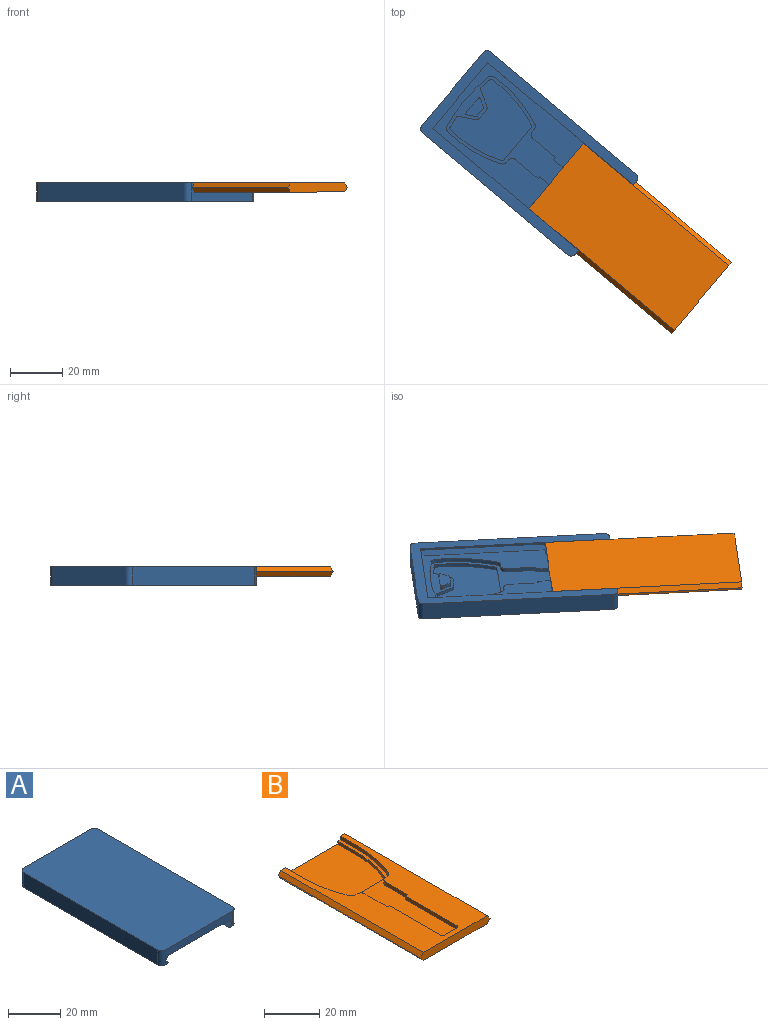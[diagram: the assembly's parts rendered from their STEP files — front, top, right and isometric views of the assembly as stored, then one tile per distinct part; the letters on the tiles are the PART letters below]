
ASSEMBLY  parts=2 mates=1
PART A: 63 faces, bbox 40.5x76.7x7 mm
  f0: plane 36.5x7mm, normal (0,-1,0), area 135.6mm2, adj f1,f5,f6,f55,f56,f57,f58,f59
  f1: plane 76.7x40.5mm, normal (0,0,-1), area 713.4mm2, adj f0,f2,f3,f4,f54,f56,f58,f59
  f2: plane 72.7x7mm, normal (-1,0,0), area 508.9mm2, adj f1,f5,f61,f62
  f3: plane 72.7x7mm, normal (1,0,0), area 508.9mm2, adj f1,f5,f59,f60
  f4: plane 36.5x7mm, normal (0,1,0), area 255.5mm2, adj f1,f5,f60,f61
  f5: plane 76.7x40.5mm, normal (0,0,1), area 3102.9mm2, adj f0,f2,f3,f4,f59,f60,f61,f62
  f6: plane 72.85x32.8mm, normal (0,0,-1), area 1328.2mm2, adj f0,f7,f8,f9,f10,f11,f12,f13
  f7: cylinder r=62.21mm len=24.24mm, axis (0,0,-1), area 37.8mm2, adj f6,f8,f34,f35
  f8: cylinder r=2.1mm len=1.9mm, axis (0,0,-1), area 4.2mm2, adj f6,f7,f9,f35
  f9: cylinder r=50.1mm len=23.22mm, axis (0,0,-1), area 36.8mm2, adj f6,f8,f10,f35
  f10: cylinder r=2.1mm len=1.94mm, axis (0,0,-1), area 3.8mm2, adj f6,f9,f11,f35
  f11: plane 1.55x0.95mm, normal (0,1,0), area 1.5mm2, adj f6,f10,f12,f35
  f12: cylinder r=1.9mm len=1.9mm, axis (0,0,-1), area 4.6mm2, adj f6,f11,f13,f35
  f13: plane 11.4x1.55mm, normal (1,0,0), area 17.7mm2, adj f6,f12,f14,f35
  f14: plane 1.55x1.05mm, normal (0,1,0), area 1.6mm2, adj f6,f13,f15,f35
  f15: plane 26.1x1.55mm, normal (1,0,0), area 40.5mm2, adj f6,f14,f16,f35
  f16: cylinder r=1.1mm len=1.55mm, axis (0,0,-1), area 2.7mm2, adj f6,f15,f17,f35
  f17: plane 6.2x1.55mm, normal (0,1,0), area 9.6mm2, adj f6,f16,f18,f35
  f18: cylinder r=1.1mm len=1.55mm, axis (0,0,-1), area 2.7mm2, adj f6,f17,f19,f35
  f19: plane 26.1x1.55mm, normal (-1,0,0), area 40.5mm2, adj f6,f18,f20,f35
  f20: plane 1.55x1.05mm, normal (0,1,0), area 1.6mm2, adj f6,f19,f21,f35
  f21: plane 11.4x1.55mm, normal (-1,0,0), area 17.7mm2, adj f6,f20,f22,f35
  f22: cylinder r=1.9mm len=1.9mm, axis (0,0,-1), area 4.6mm2, adj f6,f21,f23,f35
  f23: plane 1.55x0.95mm, normal (0,1,0), area 1.5mm2, adj f6,f22,f24,f35
  f24: cylinder r=2.1mm len=1.94mm, axis (0,0,-1), area 3.8mm2, adj f6,f23,f25,f35
  f25: cylinder r=50.1mm len=23.22mm, axis (0,0,-1), area 36.8mm2, adj f6,f24,f34,f35
  f26: cylinder r=0.4mm len=1.55mm, axis (0,0,-1), area 1.2mm2, adj f27,f33,f35,f53
  f27: cylinder r=58.77mm len=7.42mm, axis (0,0,-1), area 11.5mm2, adj f26,f28,f35,f53
  f28: cylinder r=0.4mm len=1.55mm, axis (0,0,-1), area 1.2mm2, adj f27,f29,f35,f53
  f29: plane 3.18x1.76mm, normal (0.88,-0.48,0), area 5.6mm2, adj f28,f30,f35,f53
  f30: cylinder r=0.4mm len=1.55mm, axis (0,0,-1), area 0.7mm2, adj f29,f31,f35,f53
  f31: plane 3.85x1.55mm, normal (0,-1,0), area 6mm2, adj f30,f32,f35,f53
  f32: cylinder r=0.4mm len=1.55mm, axis (0,0,-1), area 0.7mm2, adj f31,f33,f35,f53
  f33: plane 3.18x1.76mm, normal (-0.88,-0.48,0), area 5.6mm2, adj f26,f32,f35,f53
  f34: cylinder r=2.1mm len=1.9mm, axis (0,0,-1), area 4.2mm2, adj f6,f7,f25,f35
  f35: plane 68.1x27.9mm, normal (0,0,-1), area 539mm2, adj f7,f8,f9,f10,f11,f12,f13,f14
  f36: cylinder r=60.91mm len=4.59mm, axis (0,0,-1), area 6mm2, adj f35,f37,f51,f52
  f37: cylinder r=0.8mm len=1.3mm, axis (0,0,-1), area 1.4mm2, adj f35,f36,f38,f52
  f38: cylinder r=48.8mm len=22.62mm, axis (0,0,-1), area 30.1mm2, adj f35,f37,f39,f52
  f39: cylinder r=0.8mm len=1.3mm, axis (0,0,-1), area 1.2mm2, adj f35,f38,f40,f52
  f40: plane 16.2x1.3mm, normal (0,1,0), area 21.1mm2, adj f35,f39,f41,f52
  f41: cylinder r=0.8mm len=1.3mm, axis (0,0,-1), area 1.2mm2, adj f35,f40,f42,f52
  f42: cylinder r=48.8mm len=22.62mm, axis (0,0,-1), area 30.1mm2, adj f35,f41,f43,f52
  f43: cylinder r=0.8mm len=1.3mm, axis (0,0,-1), area 1.4mm2, adj f35,f42,f44,f52
  f44: cylinder r=60.91mm len=4.59mm, axis (0,0,-1), area 6mm2, adj f35,f43,f45,f52
  f45: cylinder r=0.6mm len=1.3mm, axis (0,0,-1), area 0.9mm2, adj f35,f44,f46,f52
  f46: plane 5.92x3.27mm, normal (0.88,-0.48,0), area 8.8mm2, adj f35,f45,f47,f52
  f47: cylinder r=1.7mm len=1.49mm, axis (0,0,-1), area 2.4mm2, adj f35,f46,f48,f52
  f48: plane 3.85x1.3mm, normal (0,-1,0), area 5mm2, adj f35,f47,f49,f52
  f49: cylinder r=1.7mm len=1.49mm, axis (0,0,-1), area 2.4mm2, adj f35,f48,f50,f52
  f50: plane 5.92x3.27mm, normal (-0.88,-0.48,0), area 8.8mm2, adj f35,f49,f51,f52
  f51: cylinder r=0.6mm len=1.3mm, axis (0,0,-1), area 0.9mm2, adj f35,f36,f50,f52
  f52: plane 25.3x24.57mm, normal (0,0,-1), area 496mm2, adj f36,f37,f38,f39,f40,f41,f42,f43
  f53: plane 8.17x4.1mm, normal (0,0,-1), area 26.3mm2, adj f26,f27,f28,f29,f30,f31,f32,f33
  f54: plane 35.74x3.5mm, normal (0,-1,0), area 119.9mm2, adj f1,f6,f55,f56,f57,f58
  f55: plane 72.85x1.75mm, normal (0.77,0,-0.64), area 166.4mm2, adj f0,f6,f54,f56
  f56: plane 72.85x1.75mm, normal (0.77,0,0.64), area 166.4mm2, adj f0,f1,f54,f55
  f57: plane 72.85x1.75mm, normal (-0.77,0,-0.64), area 166.4mm2, adj f0,f6,f54,f58
  f58: plane 72.85x1.75mm, normal (-0.77,0,0.64), area 166.4mm2, adj f0,f1,f54,f57
  f59: cylinder r=2mm len=7mm, axis (0,0,1), area 22mm2, adj f0,f1,f3,f5
  f60: cylinder r=2mm len=7mm, axis (0,0,-1), area 22mm2, adj f1,f3,f4,f5
  f61: cylinder r=2mm len=7mm, axis (0,0,1), area 22mm2, adj f1,f2,f4,f5
  f62: cylinder r=2mm len=7mm, axis (0,0,-1), area 22mm2, adj f0,f1,f2,f5
PART B: 36 faces, bbox 35.4x72.7x3.5 mm
  f0: cylinder r=50.1mm len=19.41mm, axis (0,0,-1), area 30.9mm2, adj f5,f6,f22,f31
  f1: cylinder r=48.8mm len=18.91mm, axis (0,0,-1), area 25.2mm2, adj f22,f23,f27,f30
  f2: plane 35.44x3.5mm, normal (0,1,0), area 42.8mm2, adj f4,f5,f22,f23,f28,f29,f30,f31
  f3: plane 35.44x3.5mm, normal (0,-1,0), area 118.9mm2, adj f4,f5,f32,f33,f34,f35
  f4: plane 72.7x32.5mm, normal (0,0,-1), area 2362.7mm2, adj f2,f3,f33,f34
  f5: plane 72.7x32.5mm, normal (0,0,1), area 1220.7mm2, adj f0,f2,f3,f6,f7,f8,f9,f10
  f6: cylinder r=2.1mm len=1.94mm, axis (0,0,-1), area 3.8mm2, adj f0,f5,f7,f22
  f7: plane 1.55x0.95mm, normal (0,1,0), area 1.5mm2, adj f5,f6,f8,f22
  f8: cylinder r=1.9mm len=1.9mm, axis (0,0,-1), area 4.6mm2, adj f5,f7,f9,f22
  f9: plane 11.4x1.55mm, normal (1,0,0), area 17.7mm2, adj f5,f8,f10,f22
  f10: plane 1.55x1.05mm, normal (0,1,0), area 1.6mm2, adj f5,f9,f11,f22
  f11: plane 26.1x1.55mm, normal (1,0,0), area 40.5mm2, adj f5,f10,f12,f22
  f12: cylinder r=1.1mm len=1.55mm, axis (0,0,-1), area 2.7mm2, adj f5,f11,f13,f22
  f13: plane 6.2x1.55mm, normal (0,1,0), area 9.6mm2, adj f5,f12,f14,f22
  f14: cylinder r=1.1mm len=1.55mm, axis (0,0,-1), area 2.7mm2, adj f5,f13,f15,f22
  f15: plane 26.1x1.55mm, normal (-1,0,0), area 40.5mm2, adj f5,f14,f16,f22
  f16: plane 1.55x1.05mm, normal (0,1,0), area 1.6mm2, adj f5,f15,f17,f22
  f17: plane 11.4x1.55mm, normal (-1,0,0), area 17.7mm2, adj f5,f16,f18,f22
  f18: cylinder r=1.9mm len=1.9mm, axis (0,0,-1), area 4.6mm2, adj f5,f17,f19,f22
  f19: plane 1.55x0.95mm, normal (0,1,0), area 1.5mm2, adj f5,f18,f20,f22
  f20: cylinder r=2.1mm len=1.94mm, axis (0,0,-1), area 3.8mm2, adj f5,f19,f21,f22
  f21: cylinder r=50.1mm len=19.41mm, axis (0,0,-1), area 30.9mm2, adj f5,f20,f22,f28
  f22: plane 70.4x27.9mm, normal (0,0,1), area 469.7mm2, adj f0,f1,f2,f6,f7,f8,f9,f10
  f23: plane 28.6x25.3mm, normal (0,0,1), area 672.4mm2, adj f1,f2,f24,f25,f26,f27,f29,f30
  f24: cylinder r=48.8mm len=18.91mm, axis (0,0,-1), area 25.2mm2, adj f22,f23,f25,f29
  f25: cylinder r=0.8mm len=1.3mm, axis (0,0,-1), area 1.2mm2, adj f22,f23,f24,f26
  f26: plane 16.2x1.3mm, normal (0,1,0), area 21.1mm2, adj f22,f23,f25,f27
  f27: cylinder r=0.8mm len=1.3mm, axis (0,0,-1), area 1.2mm2, adj f1,f22,f23,f26
  f28: plane 9.2x1.55mm, normal (-1,0,0), area 14.3mm2, adj f2,f5,f21,f22
  f29: plane 9.2x1.3mm, normal (-1,0,0), area 12mm2, adj f2,f22,f23,f24
  f30: plane 9.2x1.3mm, normal (1,0,0), area 12mm2, adj f1,f2,f22,f23
  f31: plane 9.2x1.55mm, normal (1,0,0), area 14.3mm2, adj f0,f2,f5,f22
  f32: plane 72.7x1.75mm, normal (-0.77,0,0.64), area 166.1mm2, adj f2,f3,f5,f33
  f33: plane 72.7x1.75mm, normal (-0.77,0,-0.64), area 166.1mm2, adj f2,f3,f4,f32
  f34: plane 72.7x1.75mm, normal (0.77,0,-0.64), area 166.1mm2, adj f2,f3,f4,f35
  f35: plane 72.7x1.75mm, normal (0.77,0,0.64), area 166.1mm2, adj f2,f3,f5,f34
PLACE A rot(axis=(-0.42,0.91,0),180deg) t=(52.06,-65.05,73.89)mm fixed
PLACE B rot(axis=(-0.42,0.91,0),180deg) t=(88.71,-95.8,73.89)mm
MATE slider B.f3 <-> A.f0  axis (0.77,-0.64,0) through (126.58,-150.7,75.64)mm
